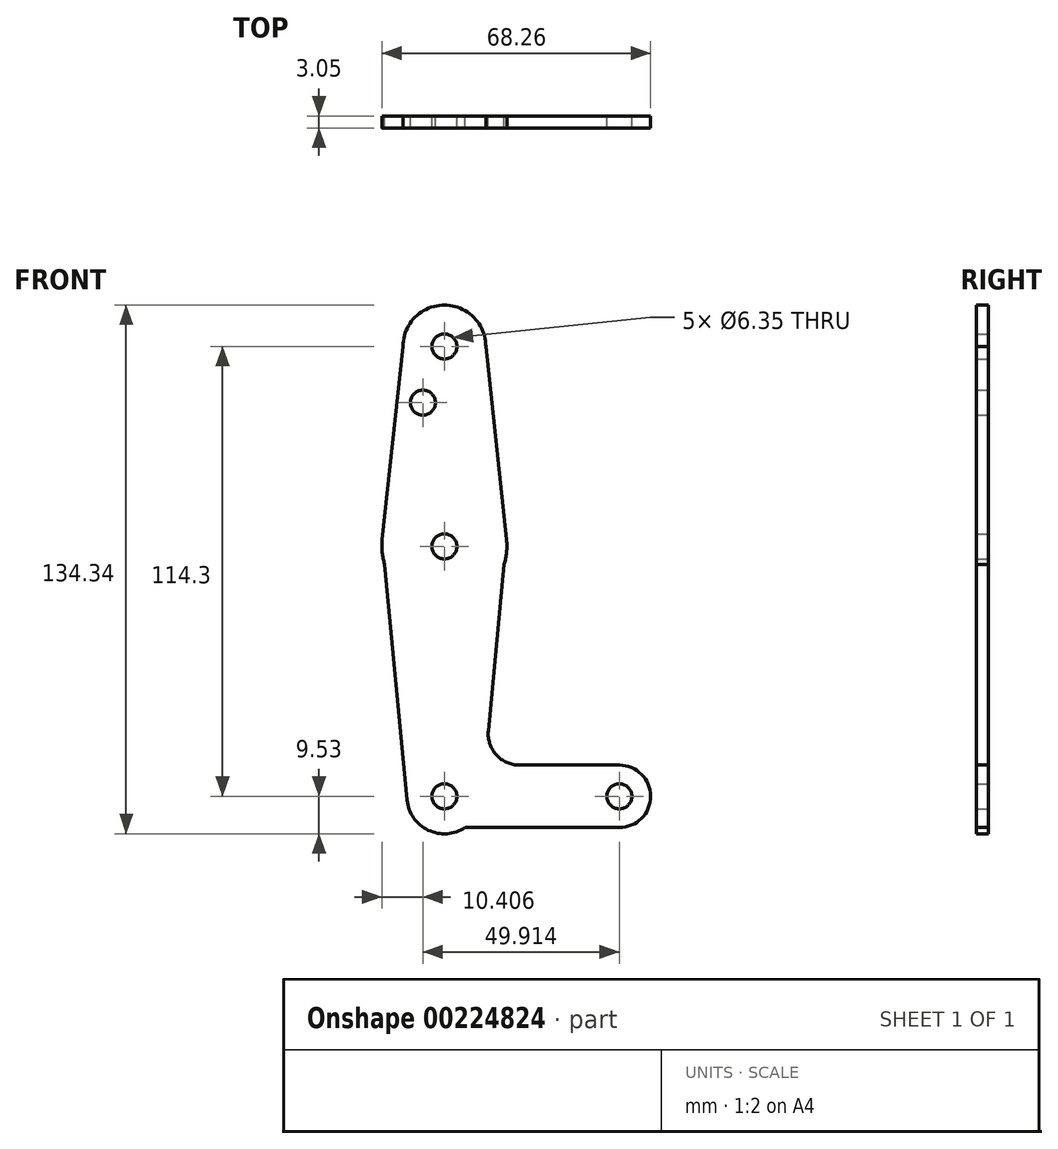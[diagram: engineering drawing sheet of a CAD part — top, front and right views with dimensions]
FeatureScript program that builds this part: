
annotation { "Feature Type Name" : "Feature", "Feature Type Description" : "" }
export const myFeature = defineFeature(function(context is Context, id is Id, definition is map)
    precondition{}
    {
        {
            var Q0;
            Q0=qCreatedBy(makeId("Front.planeOp"),FACE);
            var sketch = newSketch(context, id + "F0", { "sketchPlane" : qUnion([Q0])});
            skCircle(sketch, "E0", {"center": v(0, 0) * mm, "radius": 15.88 * mm});
            skCircle(sketch, "E1", {"center": v(0, 50.8) * mm, "radius": 10.5 * mm});
            skCircle(sketch, "E2", {"center": v(0, -63.5) * mm, "radius": 9.53 * mm});
            skLineSegment(sketch, "E3", {"start": v(0, 50.8) * mm, "end": v(0, 0) * mm});
            skCircle(sketch, "E4", {"center": v(44.45, -63.5) * mm, "radius": 7.94 * mm});
            skLineSegment(sketch, "E5", {"start": v(10.5, 50.76) * mm, "end": v(15.78, 1.7) * mm});
            skLineSegment(sketch, "E6", {"start": v(15.78, 1.7) * mm, "end": v(11.15, -46.86) * mm});
            skLineSegment(sketch, "E7", {"start": v(-10.5, 50.8) * mm, "end": v(-15.78, 1.7) * mm});
            skLineSegment(sketch, "E8", {"start": v(-15.78, 1.7) * mm, "end": v(-9.48, -64.4) * mm});
            skLineSegment(sketch, "E9", {"start": v(44.45, -55.56) * mm, "end": v(40.16, -56.82) * mm});
            skLineSegment(sketch, "E10", {"start": v(44.45, -71.44) * mm, "end": v(0, -71.44) * mm});
            skLineSegment(sketch, "E11", {"start": v(44.45, -55.56) * mm, "end": v(19.07, -55.56) * mm});
            skLineSegment(sketch, "E12.trimOffspring", {"start": v(9.57, -63.5) * mm, "end": v(9.53, -63.5) * mm});
            skCircle(sketch, "E13", {"center": v(0, 50.8) * mm, "radius": 3.18 * mm});
            skCircle(sketch, "E14", {"center": v(0, 0) * mm, "radius": 3.18 * mm});
            skCircle(sketch, "E15", {"center": v(0, -63.5) * mm, "radius": 3.18 * mm});
            skCircle(sketch, "E16", {"center": v(44.45, -63.5) * mm, "radius": 3.18 * mm});
            skCircle(sketch, "E17", {"center": v(-5.46, 36.53) * mm, "radius": 3.18 * mm});
            skLineSegment(sketch, "E18", {"start": v(-6.44, 0) * mm, "end": v(-6.44, 36.53) * mm});
            skArc(sketch, "E19.filletArc", {"start": v(11.15, -46.86) * mm, "mid": v(13.19, -52.96) * mm, "end": v(19.07, -55.56) * mm});
            skSolve(sketch);
        }
        {
            var Q0;
            Q0=qSketchRegion(id+"F0",true);
            extrude(context, id + "F1", {"entities" : qUnion([Q0]), "depth" : 3.05 * mm});
        }
    });
